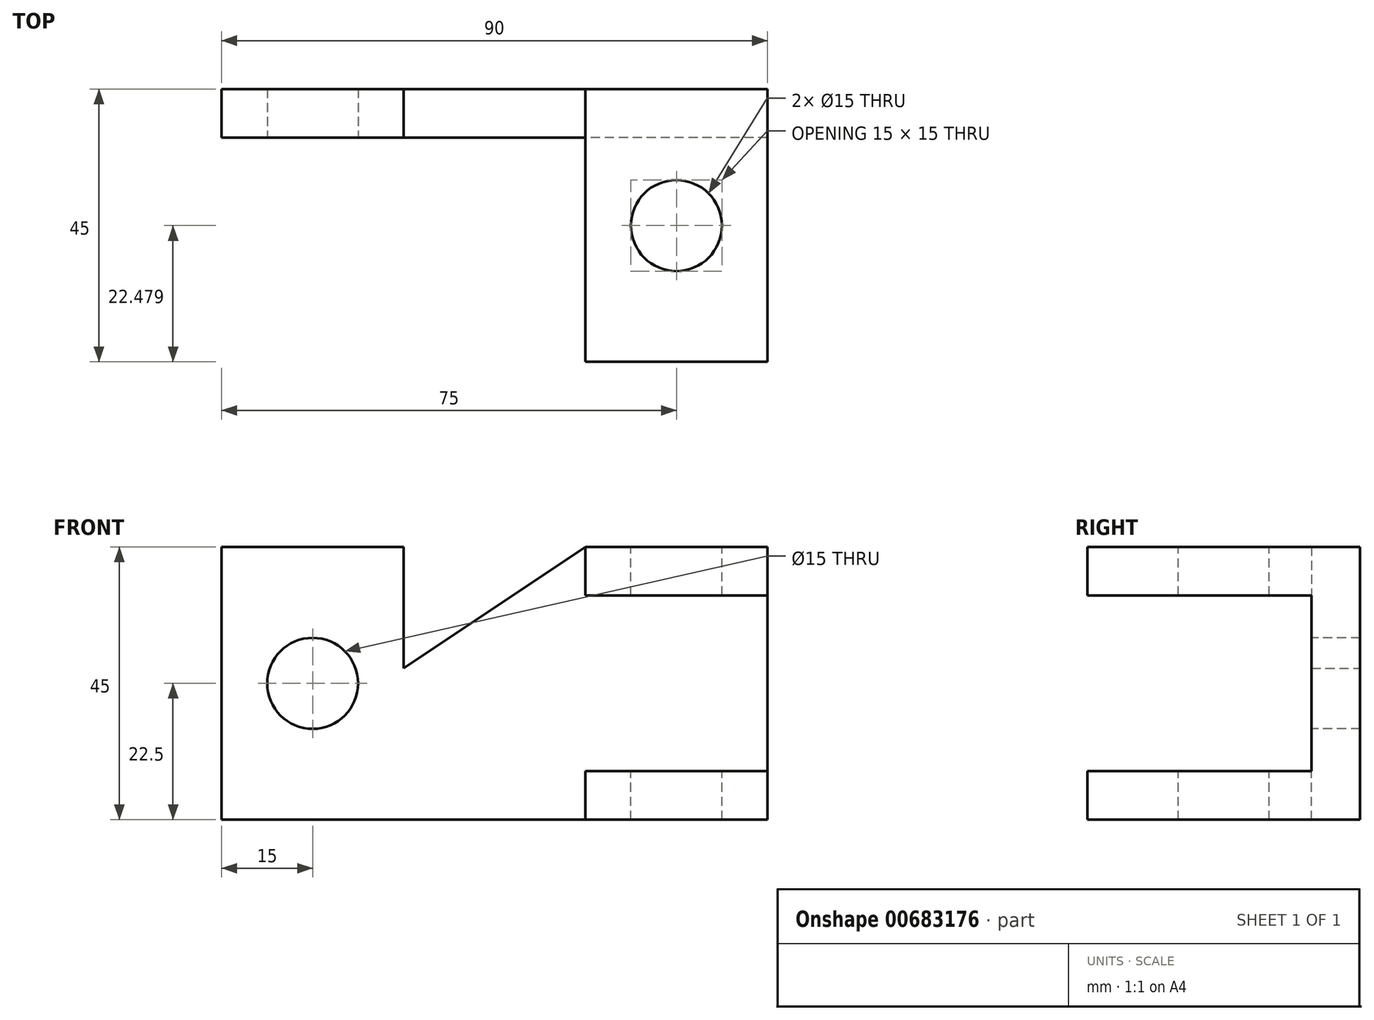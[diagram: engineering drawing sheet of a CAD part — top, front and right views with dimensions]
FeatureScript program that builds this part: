
annotation { "Feature Type Name" : "Feature", "Feature Type Description" : "" }
export const myFeature = defineFeature(function(context is Context, id is Id, definition is map)
    precondition{}
    {
        {
            var Q0;
            Q0=qCreatedBy(makeId("Front.planeOp"),FACE);
            var sketch = newSketch(context, id + "F0", { "sketchPlane" : qUnion([Q0])});
            skLineSegment(sketch, "E0.bottom", {"start": v(0, 0) * mm, "end": v(90, 0) * mm});
            skLineSegment(sketch, "E0.left", {"start": v(0, 0) * mm, "end": v(0, 45) * mm});
            skLineSegment(sketch, "E0.right", {"start": v(90, 0) * mm, "end": v(90, 45) * mm});
            skLineSegment(sketch, "E1", {"start": v(0, 45) * mm, "end": v(30, 45) * mm});
            skLineSegment(sketch, "E2", {"start": v(30, 45) * mm, "end": v(30, 25) * mm});
            skLineSegment(sketch, "E3", {"start": v(30, 25) * mm, "end": v(60, 45) * mm});
            skLineSegment(sketch, "E4", {"start": v(60, 45) * mm, "end": v(90, 45) * mm});
            skSolve(sketch);
        }
        {
            var Q0;
            Q0 = qSketchRegion(id + "F0", true);
            extrude(context, id + "F1", {"entities" : qUnion([Q0]), "depth" : 8 * mm, "offsetDistance" : 25.4 * mm});
        }
        {
            var Q0;
            Q0=makeQuery(id+"F1.opExtrude","CAP_FACE",FACE,{"disambiguationData":[OSD([sQuery(id+"F0.wireOp",EDGE,"E0.bottom"),sQuery(id+"F0.wireOp",EDGE,"E0.left"),sQuery(id+"F0.wireOp",EDGE,"E0.right"),sQuery(id+"F0.wireOp",EDGE,"E1"),sQuery(id+"F0.wireOp",EDGE,"E2"),sQuery(id+"F0.wireOp",EDGE,"E3"),sQuery(id+"F0.wireOp",EDGE,"E4")])],"isStart":false});
            var sketch = newSketch(context, id + "F2", { "sketchPlane" : qUnion([Q0])});
            skLineSegment(sketch, "E5.bottom", {"start": v(90, 45) * mm, "end": v(60, 45) * mm});
            skLineSegment(sketch, "E5.top", {"start": v(90, 37) * mm, "end": v(60, 37) * mm});
            skLineSegment(sketch, "E5.left", {"start": v(90, 45) * mm, "end": v(90, 37) * mm});
            skLineSegment(sketch, "E5.right", {"start": v(60, 45) * mm, "end": v(60, 37) * mm});
            skLineSegment(sketch, "E6.bottom", {"start": v(90, 0) * mm, "end": v(60, 0) * mm});
            skLineSegment(sketch, "E6.top", {"start": v(90, 8) * mm, "end": v(60, 8) * mm});
            skLineSegment(sketch, "E6.left", {"start": v(90, 0) * mm, "end": v(90, 8) * mm});
            skLineSegment(sketch, "E6.right", {"start": v(60, 0) * mm, "end": v(60, 8) * mm});
            skSolve(sketch);
        }
        {
            var Q0;
            Q0=makeQuery(id+"F2.imprint","IMPRINT",FACE,{"disambiguationData":[TD([[makeQuery(id+"F2.imprint","IMPRINT",EDGE,{"derivedFrom":sQuery(id+"F2.wireOp",EDGE,"E6.bottom")}),1.0]])]});
            var Q1;
            Q1=makeQuery(id+"F2.imprint","IMPRINT",FACE,{"disambiguationData":[TD([[makeQuery(id+"F2.imprint","IMPRINT",EDGE,{"derivedFrom":sQuery(id+"F2.wireOp",EDGE,"E5.bottom")}),-1.0]])]});
            extrude(context, id + "F3", {"entities" : qUnion([Q0, Q1]), "operationType" : NewBodyOperationType.ADD, "depth" : 37 * mm, "offsetDistance" : 25.4 * mm});
        }
        {
            var Q0;
            Q0=makeQuery(id+"F3.boolean.opBoolean","MERGE",FACE,{"derivedFrom":[makeQuery(id+"F1.opExtrude","SWEPT_FACE",FACE,{"disambiguationData":[OSD([sQuery(id+"F0.wireOp",EDGE,"E4")])]}),makeQuery(id+"F3.opExtrude","SWEPT_FACE",FACE,{"disambiguationData":[OSD([sQuery(id+"F2.wireOp",EDGE,"E5.bottom")])]})]});
            var sketch = newSketch(context, id + "F4", { "sketchPlane" : qUnion([Q0])});
            skCircle(sketch, "E7", {"center": v(75, -22.52) * mm, "radius": 7.5 * mm});
            skPoint(sketch, "E7.centerSnap0", {"position": v(60, -22.52) * mm});
            skSolve(sketch);
        }
        {
            var Q0;
            Q0 = qSketchRegion(id + "F4", true);
            extrude(context, id + "F5", {"entities" : qUnion([Q0]), "operationType" : NewBodyOperationType.REMOVE, "endBound" : BoundingType.THROUGH_ALL, "oppositeDirection" : true, "depth" : 25.4 * mm, "offsetDistance" : 25.4 * mm});
        }
        {
            var Q0;
            Q0=makeQuery(id+"F1.opExtrude","CAP_FACE",FACE,{"disambiguationData":[OSD([sQuery(id+"F0.wireOp",EDGE,"E0.bottom"),sQuery(id+"F0.wireOp",EDGE,"E0.left"),sQuery(id+"F0.wireOp",EDGE,"E0.right"),sQuery(id+"F0.wireOp",EDGE,"E1"),sQuery(id+"F0.wireOp",EDGE,"E2"),sQuery(id+"F0.wireOp",EDGE,"E3"),sQuery(id+"F0.wireOp",EDGE,"E4")])],"isStart":false});
            var sketch = newSketch(context, id + "F6", { "sketchPlane" : qUnion([Q0])});
            skCircle(sketch, "E8", {"center": v(15, 22.5) * mm, "radius": 7.5 * mm});
            skSolve(sketch);
        }
        {
            var Q0;
            Q0 = qSketchRegion(id + "F6", true);
            extrude(context, id + "F7", {"entities" : qUnion([Q0]), "operationType" : NewBodyOperationType.REMOVE, "endBound" : BoundingType.UP_TO_NEXT, "oppositeDirection" : true, "depth" : 25.4 * mm, "offsetDistance" : 25.4 * mm});
        }
    });
